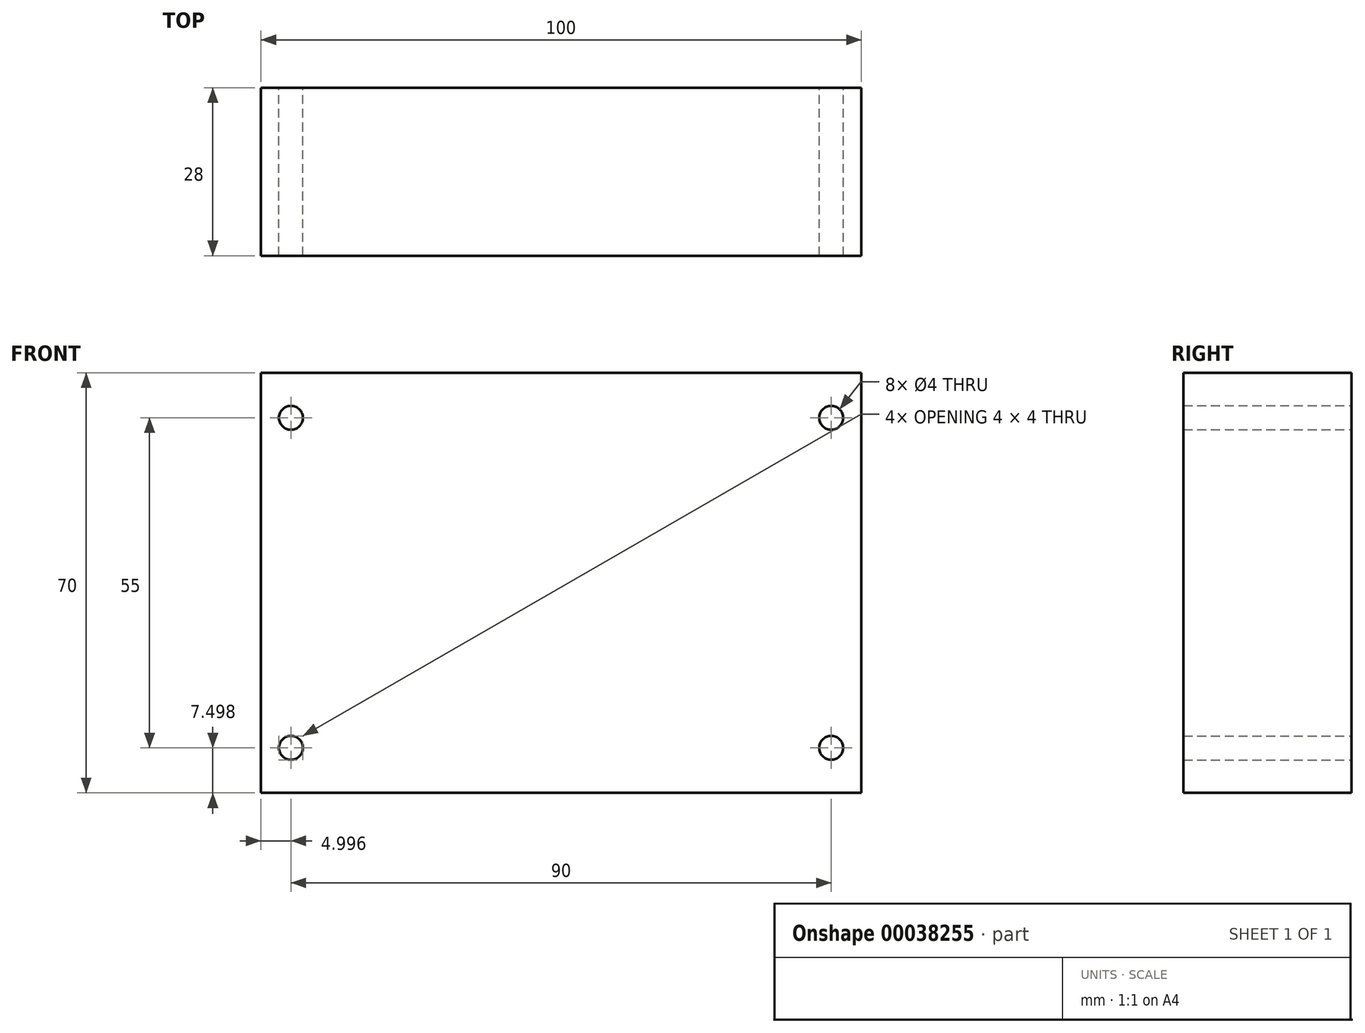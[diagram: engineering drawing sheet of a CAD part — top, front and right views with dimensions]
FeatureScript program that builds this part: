
annotation { "Feature Type Name" : "Feature", "Feature Type Description" : "" }
export const myFeature = defineFeature(function(context is Context, id is Id, definition is map)
    precondition{}
    {
        {
            var Q0;
            Q0=qCreatedBy(makeId("Front.planeOp"),FACE);
            var sketch = newSketch(context, id + "F0", { "sketchPlane" : qUnion([Q0])});
            skLineSegment(sketch, "E0.bottom", {"start": v(-123.04, -73.92) * mm, "end": v(-23.04, -73.92) * mm});
            skLineSegment(sketch, "E0.top", {"start": v(-123.04, -3.92) * mm, "end": v(-23.04, -3.92) * mm});
            skLineSegment(sketch, "E0.left", {"start": v(-123.04, -73.92) * mm, "end": v(-123.04, -3.92) * mm});
            skLineSegment(sketch, "E0.right", {"start": v(-23.04, -73.92) * mm, "end": v(-23.04, -3.92) * mm});
            skLineSegment(sketch, "E1", {"start": v(-135.49, -11.42) * mm, "end": v(-11.55, -11.42) * mm});
            skLineSegment(sketch, "E2", {"start": v(-139.47, -66.42) * mm, "end": v(-7.57, -66.42) * mm});
            skLineSegment(sketch, "E3", {"start": v(-118.04, 11.53) * mm, "end": v(-118.04, -99.56) * mm});
            skLineSegment(sketch, "E4", {"start": v(-28.04, 13.36) * mm, "end": v(-28.04, -105.07) * mm});
            skPoint(sketch, "E5", {"position": v(-118.04, -11.42) * mm});
            skPoint(sketch, "E6", {"position": v(-28.04, -11.42) * mm});
            skPoint(sketch, "E7", {"position": v(-118.04, -66.42) * mm});
            skPoint(sketch, "E8", {"position": v(-28.04, -66.42) * mm});
            skSolve(sketch);
        }
        {
            var Q0;
            {var subQ3=sQuery(id+"F0.wireOp",EDGE,"E1");var subQ5=sQuery(id+"F0.wireOp",EDGE,"E3");var subQ7=makeQuery(id+"F0.imprint","INTERSECT",VERTEX,{"derivedFrom":[subQ3,subQ5]});Q0=makeQuery(id+"F0.imprint","IMPRINT",FACE,{"disambiguationData":[TD([[makeQuery(id+"F0.imprint","IMPRINT",EDGE,{"disambiguationData":[TD([[subQ7,-1.0]])],"derivedFrom":subQ3}),-1.0]])]});}
            var Q1;
            {var subQ0=sQuery(id+"F0.wireOp",EDGE,"E3");var subQ3=sQuery(id+"F0.wireOp",EDGE,"E0.top");var subQ4=makeQuery(id+"F0.imprint","INTERSECT",VERTEX,{"derivedFrom":[subQ3,subQ0]});Q1=makeQuery(id+"F0.imprint","IMPRINT",FACE,{"disambiguationData":[TD([[makeQuery(id+"F0.imprint","IMPRINT",EDGE,{"disambiguationData":[TD([[subQ4,-1.0]])],"derivedFrom":subQ3}),-1.0]])]});}
            var Q2;
            {var subQ1=sQuery(id+"F0.wireOp",EDGE,"E2");var subQ5=sQuery(id+"F0.wireOp",EDGE,"E0.right");var subQ6=makeQuery(id+"F0.imprint","INTERSECT",VERTEX,{"derivedFrom":[subQ5,subQ1]});Q2=makeQuery(id+"F0.imprint","IMPRINT",FACE,{"disambiguationData":[TD([[makeQuery(id+"F0.imprint","IMPRINT",EDGE,{"disambiguationData":[TD([[subQ6,-1.0]])],"derivedFrom":subQ5}),1.0]])]});}
            var Q3;
            {var subQ3=sQuery(id+"F0.wireOp",EDGE,"E0.right");var subQ5=sQuery(id+"F0.wireOp",EDGE,"E0.top");var subQ6=makeQuery(id+"F0.imprint","INTERSECT",VERTEX,{"derivedFrom":[subQ5,subQ3]});Q3=makeQuery(id+"F0.imprint","IMPRINT",FACE,{"disambiguationData":[TD([[makeQuery(id+"F0.imprint","IMPRINT",EDGE,{"disambiguationData":[TD([[subQ6,1.0]])],"derivedFrom":subQ5}),-1.0]])]});}
            var Q4;
            {var subQ0=sQuery(id+"F0.wireOp",EDGE,"E3");var subQ3=sQuery(id+"F0.wireOp",EDGE,"E0.bottom");var subQ4=makeQuery(id+"F0.imprint","INTERSECT",VERTEX,{"derivedFrom":[subQ3,subQ0]});Q4=makeQuery(id+"F0.imprint","IMPRINT",FACE,{"disambiguationData":[TD([[makeQuery(id+"F0.imprint","IMPRINT",EDGE,{"disambiguationData":[TD([[subQ4,-1.0]])],"derivedFrom":subQ3}),1.0]])]});}
            var Q5;
            {var subQ0=sQuery(id+"F0.wireOp",EDGE,"E2");var subQ3=sQuery(id+"F0.wireOp",EDGE,"E0.left");var subQ4=makeQuery(id+"F0.imprint","INTERSECT",VERTEX,{"derivedFrom":[subQ3,subQ0]});Q5=makeQuery(id+"F0.imprint","IMPRINT",FACE,{"disambiguationData":[TD([[makeQuery(id+"F0.imprint","IMPRINT",EDGE,{"disambiguationData":[TD([[subQ4,-1.0]])],"derivedFrom":subQ3}),-1.0]])]});}
            var Q6;
            {var subQ3=sQuery(id+"F0.wireOp",EDGE,"E0.left");var subQ5=sQuery(id+"F0.wireOp",EDGE,"E0.top");var subQ6=makeQuery(id+"F0.imprint","INTERSECT",VERTEX,{"derivedFrom":[subQ5,subQ3]});Q6=makeQuery(id+"F0.imprint","IMPRINT",FACE,{"disambiguationData":[TD([[makeQuery(id+"F0.imprint","IMPRINT",EDGE,{"disambiguationData":[TD([[subQ6,-1.0]])],"derivedFrom":subQ5}),-1.0]])]});}
            var Q7;
            {var subQ3=sQuery(id+"F0.wireOp",EDGE,"E0.left");var subQ5=sQuery(id+"F0.wireOp",EDGE,"E0.bottom");var subQ7=makeQuery(id+"F0.imprint","INTERSECT",VERTEX,{"derivedFrom":[subQ5,subQ3]});Q7=makeQuery(id+"F0.imprint","IMPRINT",FACE,{"disambiguationData":[TD([[makeQuery(id+"F0.imprint","IMPRINT",EDGE,{"disambiguationData":[TD([[subQ7,-1.0]])],"derivedFrom":subQ5}),1.0]])]});}
            var Q8;
            {var subQ0=sQuery(id+"F0.wireOp",EDGE,"E0.right");var subQ3=sQuery(id+"F0.wireOp",EDGE,"E0.bottom");var subQ4=makeQuery(id+"F0.imprint","INTERSECT",VERTEX,{"derivedFrom":[subQ3,subQ0]});Q8=makeQuery(id+"F0.imprint","IMPRINT",FACE,{"disambiguationData":[TD([[makeQuery(id+"F0.imprint","IMPRINT",EDGE,{"disambiguationData":[TD([[subQ4,1.0]])],"derivedFrom":subQ3}),1.0]])]});}
            extrude(context, id + "F1", {"entities" : qUnion([Q0, Q1, Q2, Q3, Q4, Q5, Q6, Q7, Q8]), "depth" : 28 * mm});
        }
        {
            var Q0;
            Q0=sQuery(id+"F0.wireOp",VERTEX,"E5");
            var Q1;
            Q1=sQuery(id+"F0.wireOp",VERTEX,"E6");
            var Q2;
            Q2=sQuery(id+"F0.wireOp",VERTEX,"E7");
            var Q3;
            Q3=sQuery(id+"F0.wireOp",VERTEX,"E8");
            var Q4;
            Q4=makeQuery(id+"F1.opExtrude","SWEPT_BODY",BODY,{"disambiguationData":[OSD([sQuery(id+"F0.wireOp",EDGE,"E0.bottom"),sQuery(id+"F0.wireOp",EDGE,"E0.top"),sQuery(id+"F0.wireOp",EDGE,"E0.left"),sQuery(id+"F0.wireOp",EDGE,"E0.right")])]});
            hole(context, id + "F2", {"style" : HoleStyle.SIMPLE, "holeDiameter" : 4 * mm, "endStyle" : HoleEndStyle.THROUGH, "oppositeDirection" : true, "locations" : qUnion([Q0, Q1, Q2, Q3]), "scope" : qUnion([Q4])});
        }
    });
